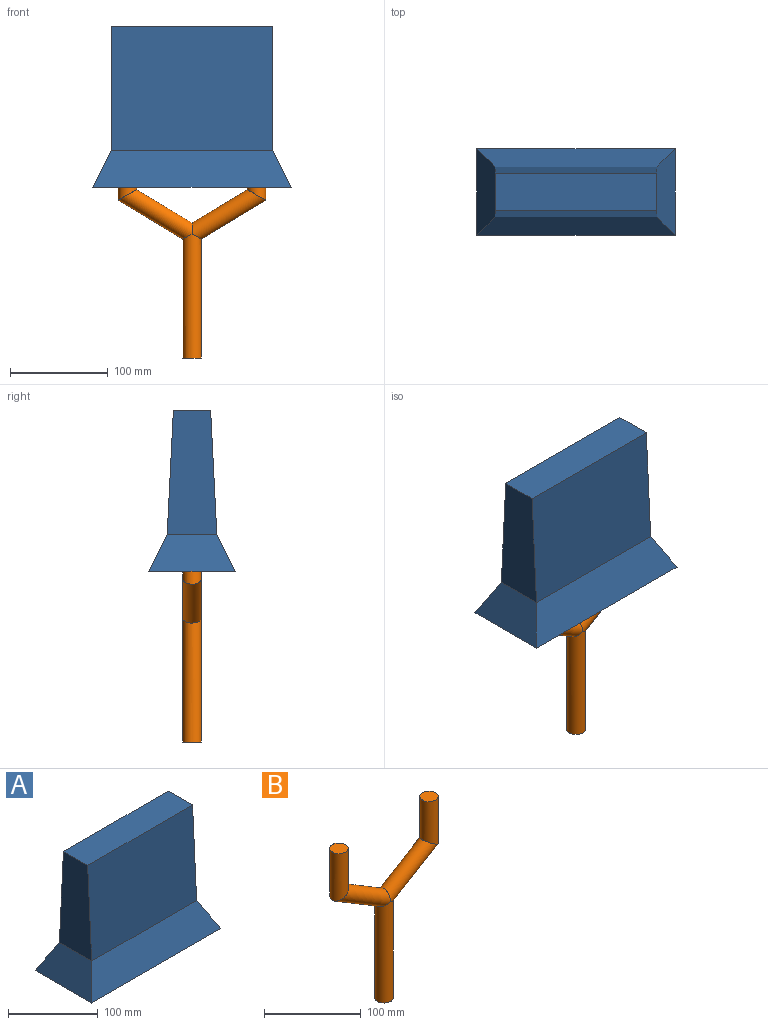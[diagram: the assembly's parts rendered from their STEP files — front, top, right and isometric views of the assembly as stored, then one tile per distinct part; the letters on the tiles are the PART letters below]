
ASSEMBLY  parts=2 mates=1
PART A: 14 faces, bbox 203.2x88.9x165.1 mm
  f0: plane 203.2x88.9mm, normal (0,0,-1), area 17494.4mm2, adj f1,f2,f3,f4,f10,f12
  f1: plane 88.9x38.1mm, normal (-0.89,0,0.45), area 2975.4mm2, adj f0,f2,f4,f6
  f2: plane 203.2x38.1mm, normal (0,-0.89,0.45), area 7844.3mm2, adj f0,f1,f3,f7
  f3: plane 88.9x38.1mm, normal (0.89,0,0.45), area 2975.4mm2, adj f0,f2,f4,f8
  f4: plane 203.2x38.1mm, normal (0,0.89,0.45), area 7844.3mm2, adj f0,f1,f3,f9
  f5: plane 165.1x38.1mm, normal (0,0,1), area 6290.3mm2, adj f6,f7,f8,f9
  f6: plane 127x50.8mm, normal (-1,0,0), area 5645.2mm2, adj f1,f5,f7,f9
  f7: plane 165.1x127mm, normal (0,-1,0.05), area 20993.9mm2, adj f2,f5,f6,f8
  f8: plane 127x50.8mm, normal (1,0,0), area 5645.2mm2, adj f3,f5,f7,f9
  f9: plane 165.1x127mm, normal (0,1,0.05), area 20993.9mm2, adj f4,f5,f6,f8
  f10: cylinder r=9.53mm len=48.26mm, axis (0,0,-1), area 2888.2mm2, adj f0,f11
  f11: plane 19.05x19.05mm, normal (0,0,-1), area 285mm2, adj f10
  f12: cylinder r=9.53mm len=48.26mm, axis (0,0,-1), area 2888.2mm2, adj f0,f13
  f13: plane 19.05x19.05mm, normal (0,0,-1), area 285mm2, adj f12
PART B: 8 faces, bbox 151.1x19.1x222.6 mm
  f0: plane 19.05x19.05mm, normal (0,0,1), area 285mm2, adj f2
  f1: plane 19.05x19.05mm, normal (0,0,-1), area 285mm2, adj f4
  f2: cylinder r=9.53mm len=61.27mm, axis (0,0,1), area 3344.3mm2, adj f0,f3
  f3: cylinder r=9.53mm len=80.47mm, axis (-0.86,0,0.52), area 4423.6mm2, adj f2,f4,f7
  f4: cylinder r=9.53mm len=127mm, axis (0,0,1), area 7417.4mm2, adj f1,f3,f7
  f5: plane 19.05x19.05mm, normal (0,0,1), area 285mm2, adj f6
  f6: cylinder r=9.53mm len=61.27mm, axis (0,0,1), area 3344.3mm2, adj f5,f7
  f7: cylinder r=9.53mm len=80.48mm, axis (0.86,0,0.52), area 4445.6mm2, adj f3,f4,f6
PLACE A t=(-97.09,-18.57,-0.73)mm
PLACE B t=(-97.09,-18.57,-48.06)mm
MATE fastened B.f2 <-> A.f12  axis (0,0,1) through (-163.13,-18.57,47.53)mm
